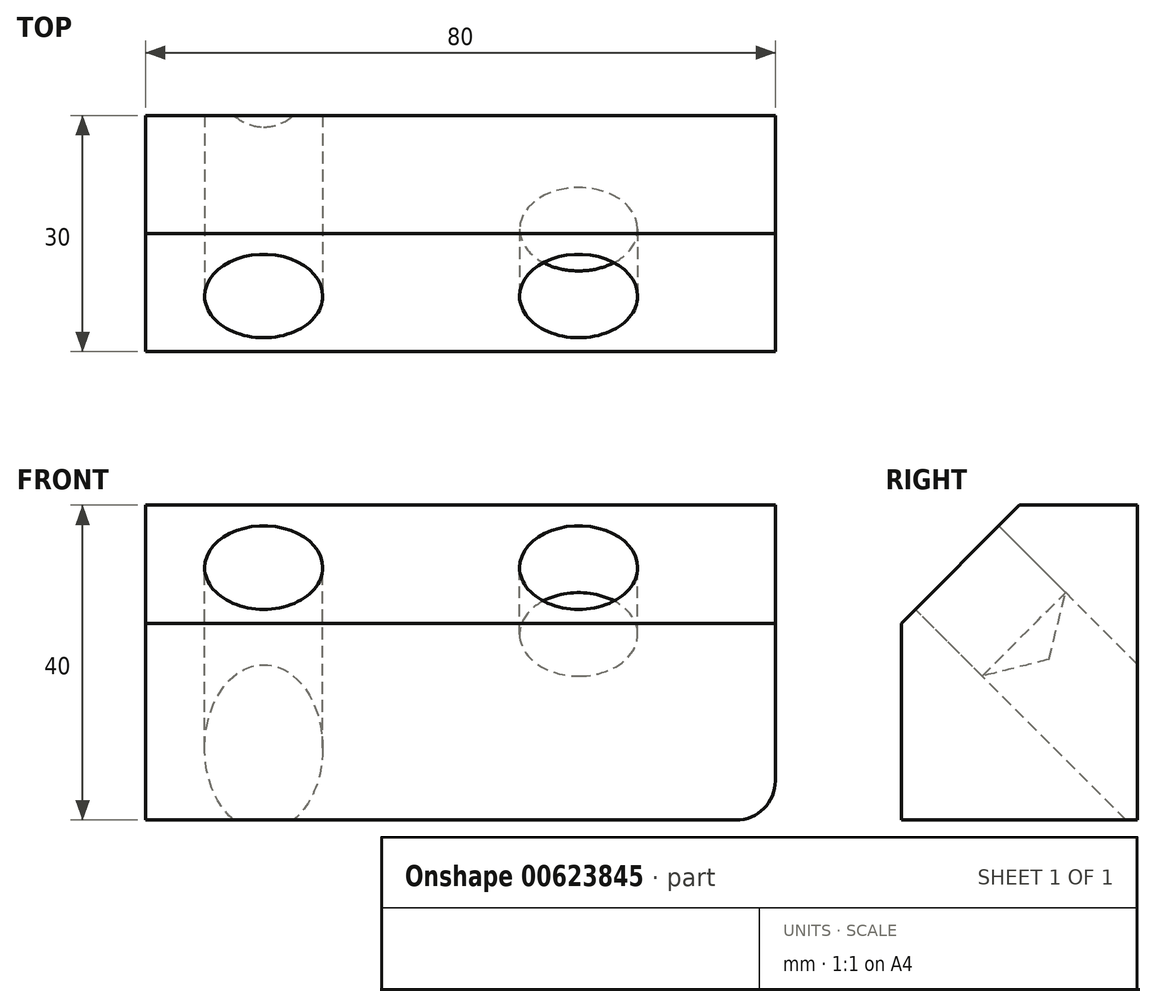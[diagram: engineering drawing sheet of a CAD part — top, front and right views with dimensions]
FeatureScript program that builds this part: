
annotation { "Feature Type Name" : "Feature", "Feature Type Description" : "" }
export const myFeature = defineFeature(function(context is Context, id is Id, definition is map)
    precondition{}
    {
        {
            var Q0;
            Q0=qCreatedBy(makeId("Top.planeOp"),FACE);
            var sketch = newSketch(context, id + "F0", { "sketchPlane" : qUnion([Q0])});
            skLineSegment(sketch, "E0.bottom", {"start": v(-80, -30) * mm, "end": v(0, -30) * mm});
            skLineSegment(sketch, "E0.top", {"start": v(-80, 0) * mm, "end": v(0, 0) * mm});
            skLineSegment(sketch, "E0.left", {"start": v(-80, -30) * mm, "end": v(-80, 0) * mm});
            skLineSegment(sketch, "E0.right", {"start": v(0, -30) * mm, "end": v(0, 0) * mm});
            skSolve(sketch);
        }
        {
            var Q0;
            Q0=makeQuery(id+"F0.imprint","IMPRINT",FACE,{"disambiguationData":[TD([[makeQuery(id+"F0.imprint","IMPRINT",EDGE,{"derivedFrom":sQuery(id+"F0.wireOp",EDGE,"E0.bottom")}),1.0]])]});
            extrude(context, id + "F1", {"entities" : qUnion([Q0]), "depth" : 40 * mm, "offsetDistance" : 25 * mm});
        }
        {
            var Q0;
            Q0=makeQuery(id+"F1.opExtrude","CAP_EDGE",EDGE,{"disambiguationData":[OSD([sQuery(id+"F0.wireOp",EDGE,"E0.bottom")])],"isStart":false});
            chamfer(context, id + "F2", {"entities" : qUnion([Q0]), "width" : 15 * mm, "tangentPropagation" : true});
        }
        {
            var Q0;
            Q0=makeQuery(id+"F2.opChamfer","BLEND_FACE",FACE,{"disambiguationData":[OSD([sQuery(id+"F0.wireOp",EDGE,"E0.bottom")])]});
            var sketch = newSketch(context, id + "F3", { "sketchPlane" : qUnion([Q0])});
            skPoint(sketch, "E1", {"position": v(-65, 6.46) * mm});
            skSolve(sketch);
        }
        {
            var Q0;
            Q0=sQuery(id+"F3.wireOp",VERTEX,"E1");
            var Q1;
            Q1=makeQuery(id+"F1.opExtrude","SWEPT_BODY",BODY,{"disambiguationData":[OSD([sQuery(id+"F0.wireOp",EDGE,"E0.bottom"),sQuery(id+"F0.wireOp",EDGE,"E0.top"),sQuery(id+"F0.wireOp",EDGE,"E0.left"),sQuery(id+"F0.wireOp",EDGE,"E0.right")])]});
            hole(context, id + "F4", {"style" : HoleStyle.SIMPLE, "endStyle" : HoleEndStyle.THROUGH, "holeDiameter" : 15 * mm, "majorDiameter" : 5 * mm, "isTappedThrough" : true, "tappedDepth" : 12 * mm, "tapClearance" : 3, "locations" : qUnion([Q0]), "scope" : qUnion([Q1])});
        }
        {
            var Q0;
            Q0=makeQuery(id+"F2.opChamfer","BLEND_FACE",FACE,{"disambiguationData":[OSD([sQuery(id+"F0.wireOp",EDGE,"E0.bottom")])]});
            var sketch = newSketch(context, id + "F5", { "sketchPlane" : qUnion([Q0])});
            skPoint(sketch, "E2", {"position": v(-25, 6.46) * mm});
            skSolve(sketch);
        }
        {
            var Q0;
            Q0=sQuery(id+"F5.wireOp",VERTEX,"E2");
            var Q1;
            Q1=makeQuery(id+"F1.opExtrude","SWEPT_BODY",BODY,{"disambiguationData":[OSD([sQuery(id+"F0.wireOp",EDGE,"E0.bottom"),sQuery(id+"F0.wireOp",EDGE,"E0.top"),sQuery(id+"F0.wireOp",EDGE,"E0.left"),sQuery(id+"F0.wireOp",EDGE,"E0.right")])]});
            hole(context, id + "F6", {"style" : HoleStyle.SIMPLE, "endStyle" : HoleEndStyle.BLIND, "holeDiameter" : 15 * mm, "majorDiameter" : 5 * mm, "holeDepth" : 12 * mm, "isTappedThrough" : true, "tappedDepth" : 12 * mm, "tapClearance" : 3, "locations" : qUnion([Q0]), "scope" : qUnion([Q1])});
        }
        {
            var Q0;
            Q0=makeQuery(id+"F1.opExtrude","CAP_EDGE",EDGE,{"disambiguationData":[OSD([sQuery(id+"F0.wireOp",EDGE,"E0.right")])],"isStart":true});
            fillet(context, id + "F7", {"entities" : qUnion([Q0]), "radius" : 5 * mm, "tangentPropagation" : true, "allowEdgeOverflow" : false});
        }
    });
